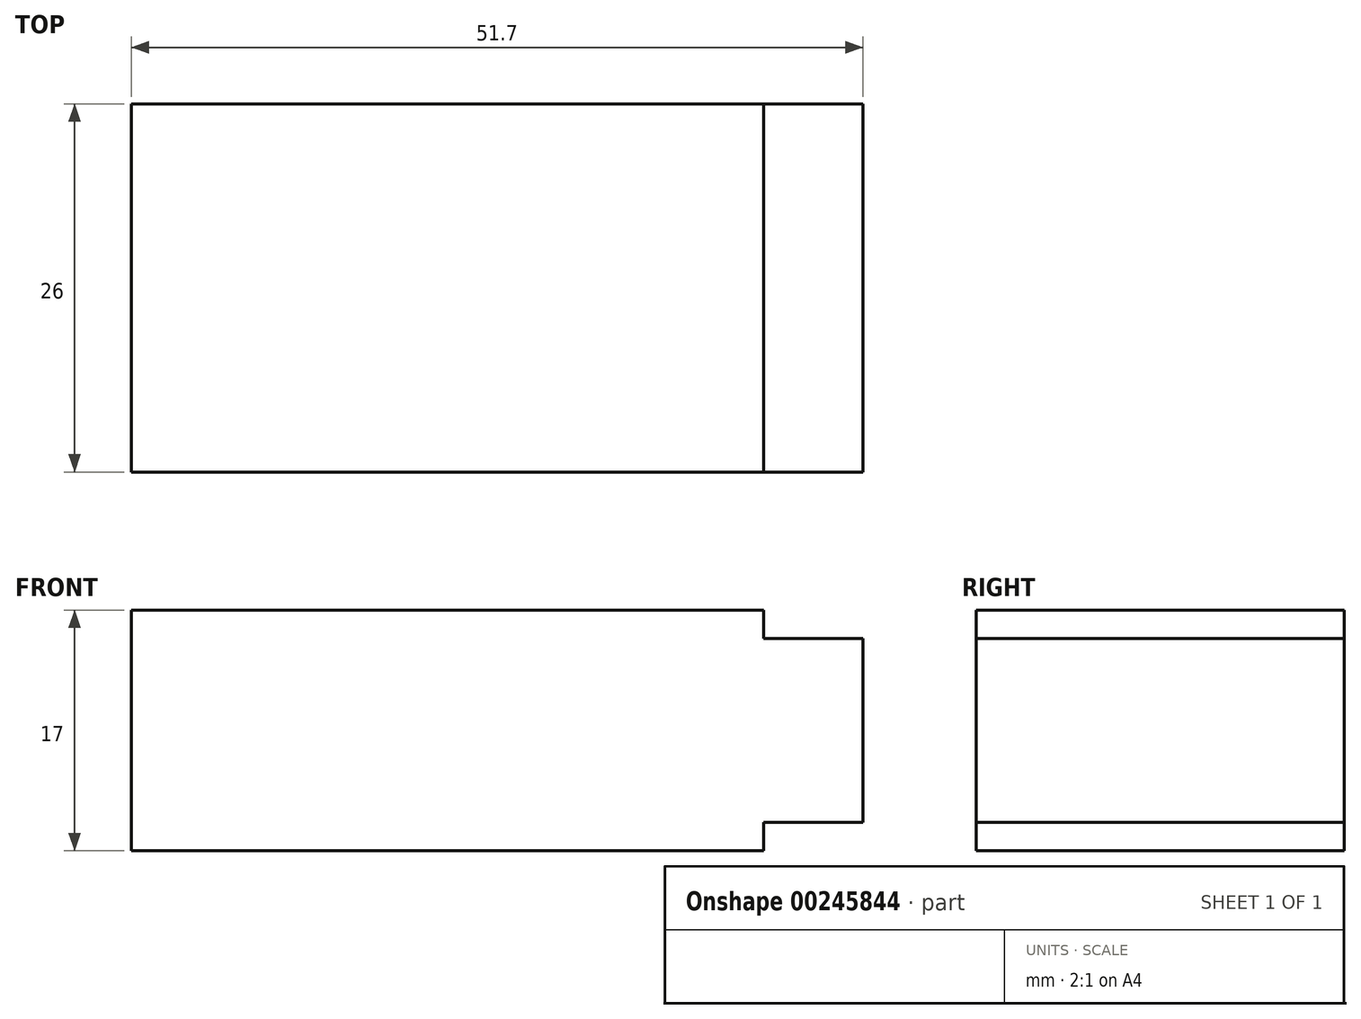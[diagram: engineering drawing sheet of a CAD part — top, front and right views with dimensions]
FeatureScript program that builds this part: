
annotation { "Feature Type Name" : "Feature", "Feature Type Description" : "" }
export const myFeature = defineFeature(function(context is Context, id is Id, definition is map)
    precondition{}
    {
        {
            var Q0;
            Q0=qCreatedBy(makeId("Top.planeOp"),FACE);
            var sketch = newSketch(context, id + "F0", { "sketchPlane" : qUnion([Q0])});
            skLineSegment(sketch, "E0.bottom", {"start": v(22.35, -13) * mm, "end": v(-22.35, -13) * mm});
            skLineSegment(sketch, "E0.top", {"start": v(22.35, 13) * mm, "end": v(-22.35, 13) * mm});
            skLineSegment(sketch, "E0.left", {"start": v(22.35, -13) * mm, "end": v(22.35, 13) * mm});
            skLineSegment(sketch, "E0.right", {"start": v(-22.35, -13) * mm, "end": v(-22.35, 13) * mm});
            skPoint(sketch, "E0.middle", {"position": v(0, 0) * mm});
            skLineSegment(sketch, "E1.bottom", {"start": v(22.35, 13) * mm, "end": v(29.35, 13) * mm});
            skLineSegment(sketch, "E1.top", {"start": v(22.35, -13) * mm, "end": v(29.35, -13) * mm});
            skLineSegment(sketch, "E1.left", {"start": v(22.35, 13) * mm, "end": v(22.35, -13) * mm});
            skLineSegment(sketch, "E1.right", {"start": v(29.35, 13) * mm, "end": v(29.35, -13) * mm});
            skSolve(sketch);
        }
        {
            var Q0;
            Q0=makeQuery(id+"F0.imprint","IMPRINT",FACE,{"disambiguationData":[TD([[makeQuery(id+"F0.imprint","IMPRINT",EDGE,{"derivedFrom":sQuery(id+"F0.wireOp",EDGE,"E0.bottom")}),-1.0]])]});
            extrude(context, id + "F1", {"entities" : qUnion([Q0]), "depth" : 17 * mm});
        }
        {
            var Q0;
            Q0=makeQuery(id+"F0.imprint","IMPRINT",FACE,{"disambiguationData":[TD([[makeQuery(id+"F0.imprint","IMPRINT",EDGE,{"derivedFrom":sQuery(id+"F0.wireOp",EDGE,"E1.bottom")}),-1.0]])]});
            extrude(context, id + "F2", {"entities" : qUnion([Q0]), "operationType" : NewBodyOperationType.ADD, "depth" : 15 * mm, "hasSecondDirection" : true, "secondDirectionOppositeDirection" : false, "secondDirectionDepth" : 2 * mm});
        }
    });
